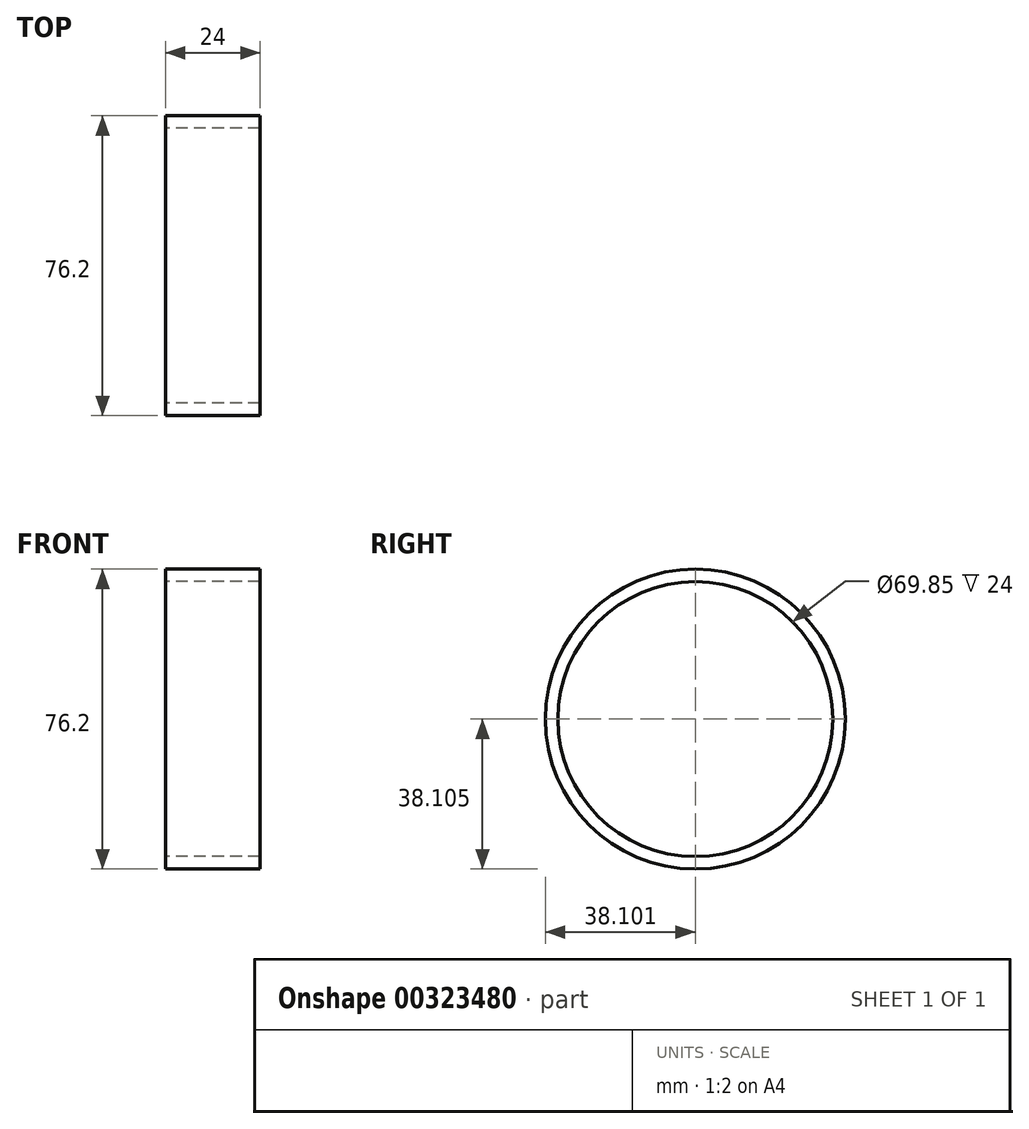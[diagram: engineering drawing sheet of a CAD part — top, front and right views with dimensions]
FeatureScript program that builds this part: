
annotation { "Feature Type Name" : "Feature", "Feature Type Description" : "" }
export const myFeature = defineFeature(function(context is Context, id is Id, definition is map)
    precondition{}
    {
        {
            assignVariable(context, id + "F0", {"name" : "length", "anyValue" : 24});
        }
        {
            var Q0;
            Q0=qCreatedBy(makeId("Right.planeOp"),FACE);
            var sketch = newSketch(context, id + "F1", { "sketchPlane" : qUnion([Q0])});
            skCircle(sketch, "E0", {"center": v(13.93, 20.1) * mm, "radius": 38.1 * mm});
            skCircle(sketch, "E1", {"center": v(13.93, 20.1) * mm, "radius": 34.93 * mm});
            skSolve(sketch);
        }
        {
            var Q0;
            Q0=makeQuery(id+"F1.imprint","IMPRINT",FACE,{"disambiguationData":[TD([[makeQuery(id+"F1.imprint","IMPRINT",EDGE,{"derivedFrom":sQuery(id+"F1.wireOp",EDGE,"E0")}),1.0]])]});
            extrude(context, id + "F2", {"entities" : qUnion([Q0]), "depth" : (getVariable(context, 'length')) * mm});
        }
    });
